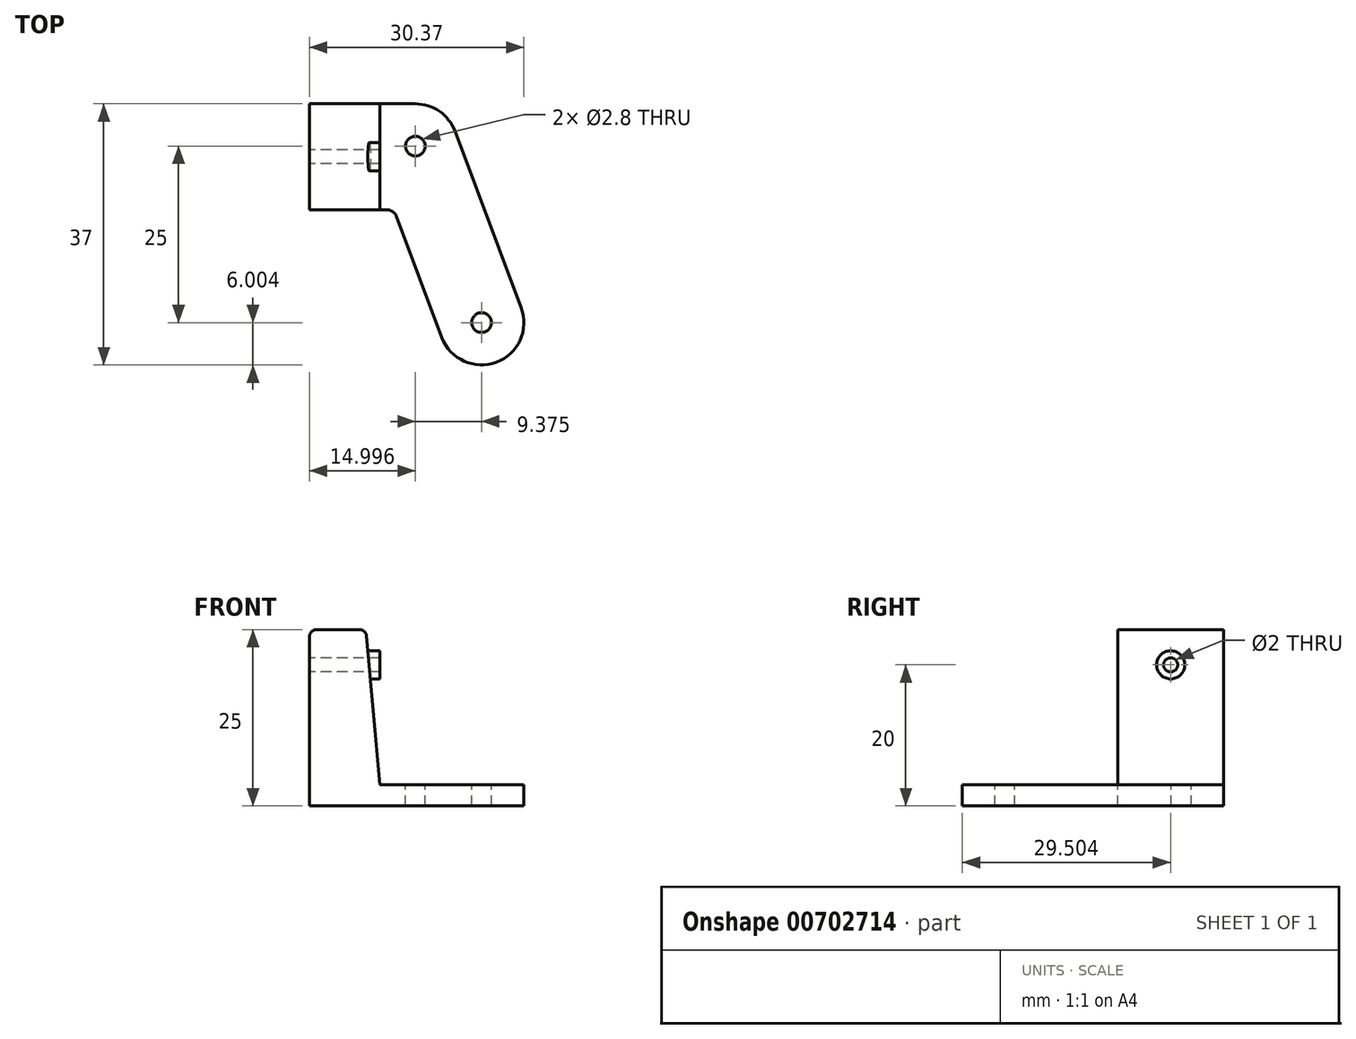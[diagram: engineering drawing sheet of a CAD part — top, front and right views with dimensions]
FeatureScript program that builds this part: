
annotation { "Feature Type Name" : "Feature", "Feature Type Description" : "" }
export const myFeature = defineFeature(function(context is Context, id is Id, definition is map)
    precondition{}
    {
        {
            var Q0;
            Q0=qCreatedBy(makeId("Top.planeOp"),FACE);
            var sketch = newSketch(context, id + "F0", { "sketchPlane" : qUnion([Q0])});
            skArc(sketch, "E0", {"start": v(4.1, -18.28) * mm, "mid": v(11.83, -21.8) * mm, "end": v(15.34, -14.07) * mm});
            skArc(sketch, "E1", {"start": v(5.96, 10.93) * mm, "mid": v(3.76, 13.76) * mm, "end": v(0.35, 14.82) * mm});
            skLineSegment(sketch, "E2", {"start": v(15.34, -14.07) * mm, "end": v(5.96, 10.93) * mm});
            skLineSegment(sketch, "E3", {"start": v(0.35, 14.82) * mm, "end": v(-14.65, 14.82) * mm});
            skLineSegment(sketch, "E4", {"start": v(-14.65, 14.82) * mm, "end": v(-14.65, -0.18) * mm});
            skLineSegment(sketch, "E5", {"start": v(9.72, -16.18) * mm, "end": v(0.35, 8.82) * mm, "construction": true});
            skLineSegment(sketch, "E6", {"start": v(4.1, -18.28) * mm, "end": v(-2.32, -1.15) * mm});
            skLineSegment(sketch, "E7", {"start": v(-14.65, -0.18) * mm, "end": v(-3.73, -0.18) * mm});
            skPoint(sketch, "E8.visualSharp", {"position": v(-2.69, -0.18) * mm});
            skArc(sketch, "E8.filletArc", {"start": v(-2.32, -1.15) * mm, "mid": v(-2.87, -0.44) * mm, "end": v(-3.73, -0.18) * mm});
            skCircle(sketch, "E9", {"center": v(0.35, 8.82) * mm, "radius": 1.4 * mm});
            skCircle(sketch, "E10", {"center": v(9.72, -16.18) * mm, "radius": 1.4 * mm});
            skLineSegment(sketch, "E11.0", {"start": v(-4.65, 14.82) * mm, "end": v(-4.65, -0.18) * mm});
            skSolve(sketch);
        }
        {
            var Q0;
            Q0=qCreatedBy(makeId("Top.planeOp"),FACE);
            cPlane(context, id + "F1", {"entities" : qUnion([Q0]), "cplaneType" : CPlaneType.OFFSET, "offset" : 22 * mm, "width" : 152.4 * mm, "height" : 152.4 * mm});
        }
        {
            var Q0;
            Q0=qCreatedBy(id+"F1.planeOp",FACE);
            var sketch = newSketch(context, id + "F2", { "sketchPlane" : qUnion([Q0])});
            skArc(sketch, "E12", {"start": v(4.1, -18.28) * mm, "mid": v(11.83, -21.8) * mm, "end": v(15.34, -14.07) * mm});
            skArc(sketch, "E13", {"start": v(5.96, 10.93) * mm, "mid": v(3.76, 13.76) * mm, "end": v(0.35, 14.82) * mm});
            skLineSegment(sketch, "E14", {"start": v(15.34, -14.07) * mm, "end": v(5.96, 10.93) * mm});
            skLineSegment(sketch, "E15", {"start": v(0.35, 14.82) * mm, "end": v(-14.65, 14.82) * mm});
            skLineSegment(sketch, "E16", {"start": v(-14.65, 14.82) * mm, "end": v(-14.65, -0.18) * mm});
            skLineSegment(sketch, "E17", {"start": v(9.72, -16.18) * mm, "end": v(0.35, 8.82) * mm, "construction": true});
            skLineSegment(sketch, "E18", {"start": v(4.1, -18.28) * mm, "end": v(-2.32, -1.15) * mm});
            skLineSegment(sketch, "E19", {"start": v(-14.65, -0.18) * mm, "end": v(-3.73, -0.18) * mm});
            skPoint(sketch, "E20.visualSharp", {"position": v(-2.69, -0.18) * mm});
            skArc(sketch, "E20.filletArc", {"start": v(-2.32, -1.15) * mm, "mid": v(-2.87, -0.44) * mm, "end": v(-3.73, -0.18) * mm});
            skCircle(sketch, "E21", {"center": v(0.35, 8.82) * mm, "radius": 1.4 * mm});
            skCircle(sketch, "E22", {"center": v(9.72, -16.18) * mm, "radius": 1.4 * mm});
            skLineSegment(sketch, "E23.0", {"start": v(-6.65, 14.82) * mm, "end": v(-6.65, -0.18) * mm});
            skSolve(sketch);
        }
        {
            var Q0;
            Q0=makeQuery(id+"F0.imprint","IMPRINT",FACE,{"disambiguationData":[TD([[makeQuery(id+"F0.imprint","IMPRINT",EDGE,{"derivedFrom":sQuery(id+"F0.wireOp",EDGE,"E0")}),1.0]])]});
            var Q1;
            {var subQ0=sQuery(id+"F0.wireOp",EDGE,"E4");Q1=makeQuery(id+"F0.imprint","IMPRINT",FACE,{"disambiguationData":[TD([[makeQuery(id+"F0.imprint","IMPRINT",EDGE,{"derivedFrom":subQ0}),1.0]])]});}
            extrude(context, id + "F3", {"entities" : qUnion([Q0, Q1]), "oppositeDirection" : true, "depth" : 3 * mm, "offsetDistance" : 25.4 * mm});
        }
        {
            var Q1;
            {var subQ0=sQuery(id+"F0.wireOp",EDGE,"E4");Q1=makeQuery(id+"F0.imprint","IMPRINT",FACE,{"disambiguationData":[TD([[makeQuery(id+"F0.imprint","IMPRINT",EDGE,{"derivedFrom":subQ0}),1.0]])]});}
            var Q2;
            {var subQ0=sQuery(id+"F2.wireOp",EDGE,"E16");Q2=makeQuery(id+"F2.imprint","IMPRINT",FACE,{"disambiguationData":[TD([[makeQuery(id+"F2.imprint","IMPRINT",EDGE,{"derivedFrom":subQ0}),1.0]])]});}
            loft(context, id + "F4", {"operationType" : NewBodyOperationType.ADD, "sheetProfilesArray" : [{ "sheetProfileEntities" : qUnion([Q1]) }, { "sheetProfileEntities" : qUnion([Q2]) }]});
        }
        {
            var Q0;
            {var subQ0=sQuery(id+"F0.wireOp",EDGE,"E4");Q0=makeQuery(id+"F4.boolean.opBoolean","MERGE",FACE,{"derivedFrom":[makeQuery(id+"F3.opExtrude","SWEPT_FACE",FACE,{"disambiguationData":[OSD([subQ0])]}),makeQuery(id+"F4.opLoft","SWEPT_FACE",FACE,{"disambiguationData":[OSD([sQuery(id+"F0.wireOp",EDGE,"E3"),subQ0,sQuery(id+"F0.wireOp",EDGE,"E7"),sQuery(id+"F2.wireOp",EDGE,"E15"),sQuery(id+"F2.wireOp",EDGE,"E16"),sQuery(id+"F2.wireOp",EDGE,"E19")])]})]});}
            var sketch = newSketch(context, id + "F5", { "sketchPlane" : qUnion([Q0])});
            skCircle(sketch, "E24", {"center": v(-7.32, 17) * mm, "radius": 1 * mm});
            skPoint(sketch, "E24.centerSnap0", {"position": v(-7.32, 22) * mm});
            skCircle(sketch, "E25", {"center": v(-7.32, 17) * mm, "radius": 2 * mm});
            skSolve(sketch);
        }
        {
            var Q0;
            Q0=makeQuery(id+"F5.imprint","IMPRINT",FACE,{"disambiguationData":[TD([[makeQuery(id+"F5.imprint","IMPRINT",EDGE,{"derivedFrom":sQuery(id+"F5.wireOp",EDGE,"E24")}),-1.0]])]});
            extrude(context, id + "F6", {"entities" : qUnion([Q0]), "operationType" : NewBodyOperationType.ADD, "oppositeDirection" : true, "depth" : 10 * mm, "offsetDistance" : 25.4 * mm});
        }
        {
            var Q0;
            Q0=makeQuery(id+"F5.imprint","IMPRINT",FACE,{"disambiguationData":[TD([[makeQuery(id+"F5.imprint","IMPRINT",EDGE,{"derivedFrom":sQuery(id+"F5.wireOp",EDGE,"E24")}),1.0]])]});
            var Q1;
            Q1=sQuery(id+"F5.wireOp",EDGE,"E24");
            extrude(context, id + "F7", {"entities" : qUnion([Q0]), "operationType" : NewBodyOperationType.REMOVE, "surfaceEntities" : qUnion([Q1]), "oppositeDirection" : true, "depth" : 15 * mm, "offsetDistance" : 25.4 * mm});
        }
        {
            var Q0;
            Q0=makeQuery(id+"F4.opLoft","MID_CAP_EDGE",EDGE,{"disambiguationData":[OSD([sQuery(id+"F2.wireOp",EDGE,"E15"),sQuery(id+"F2.wireOp",EDGE,"E19"),sQuery(id+"F2.wireOp",EDGE,"E23.0")])],"capPos":1.0});
            var Q1;
            Q1=makeQuery(id+"F4.opLoft","MID_CAP_EDGE",EDGE,{"disambiguationData":[OSD([sQuery(id+"F0.wireOp",EDGE,"E3"),sQuery(id+"F0.wireOp",EDGE,"E7"),sQuery(id+"F0.wireOp",EDGE,"E11.0")])],"capPos":0.0});
            var Q2;
            Q2=makeQuery(id+"F4.opLoft","MID_CAP_EDGE",EDGE,{"disambiguationData":[OSD([sQuery(id+"F2.wireOp",EDGE,"E15"),sQuery(id+"F2.wireOp",EDGE,"E16"),sQuery(id+"F2.wireOp",EDGE,"E19")])],"capPos":1.0});
            fillet(context, id + "F8", {"entities" : qUnion([Q0, Q1, Q2]), "radius" : 1 * mm, "tangentPropagation" : true, "allowEdgeOverflow" : false});
        }
    });
